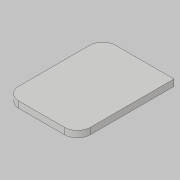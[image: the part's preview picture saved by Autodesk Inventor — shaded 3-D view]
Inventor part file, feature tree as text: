
AUTODESK INVENTOR PART (.ipt)
format: ipt  version: 2018.3 (Build 223284000, 284)  size: 111,616 bytes
history: native  units: in
note: dims shown in document units (in); Inventor stores cm internally (conversion verified against a paired STEP export)
features: fillet x3, shell x1, sketch x1
ambient origin geometry x8: Origin, YZ Plane, XZ Plane, XY Plane, X Axis, Y Axis, Z Axis, Center Point
bodies: Solid1 (feature_tree), Body (feature_tree)
feature tree (5):
  fillet  "Fillet6"  Radius=5.9055in
  fillet  "Fillet4"  Radius=4.362in
  fillet  "Fillet2"  Radius=0.3937in
  shell  "Shell2"  Thickness=0.7874in
  sketch  "Sketch1"  dims[d60=0.7874in d64=0.7874in d124=0.0787in]
